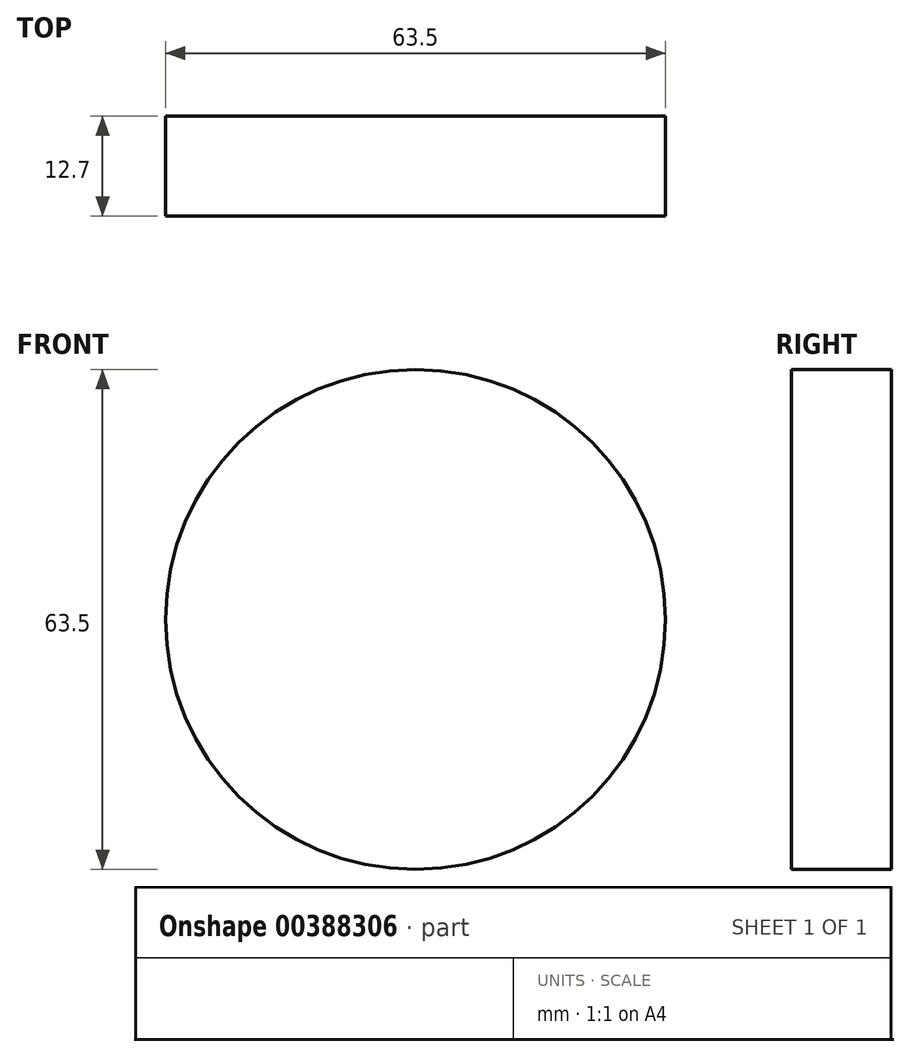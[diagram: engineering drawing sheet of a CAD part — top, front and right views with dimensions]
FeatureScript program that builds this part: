
annotation { "Feature Type Name" : "Feature", "Feature Type Description" : "" }
export const myFeature = defineFeature(function(context is Context, id is Id, definition is map)
    precondition{}
    {
        {
            var Q0;
            Q0=qCreatedBy(makeId("Front.planeOp"),FACE);
            var sketch = newSketch(context, id + "F0", { "sketchPlane" : qUnion([Q0])});
            skCircle(sketch, "E0", {"center": v(0, 0) * mm, "radius": 31.75 * mm});
            skSolve(sketch);
        }
        {
            var Q0;
            Q0=qSketchRegion(id+"F0",true);
            extrude(context, id + "F1", {"entities" : qUnion([Q0]), "depth" : 12.7 * mm});
        }
    });
